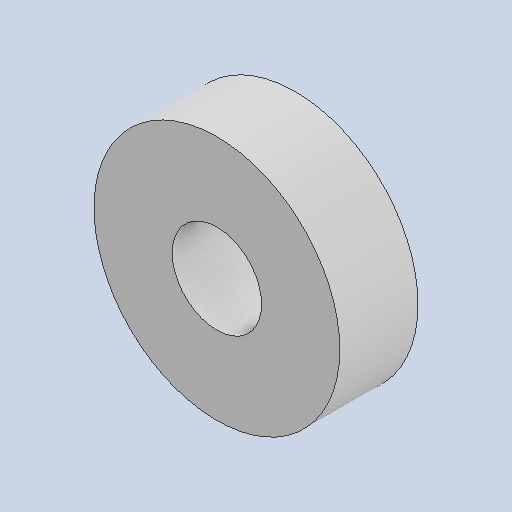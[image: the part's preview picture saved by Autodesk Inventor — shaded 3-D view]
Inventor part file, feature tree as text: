
AUTODESK INVENTOR PART (.ipt)
format: ipt  version: 2022 (Build 260153000, 153)  size: 101,376 bytes
history: native  units: in
note: dims shown in document units (in); Inventor stores cm internally (conversion verified against a paired STEP export)
features: extrude x1, sketch x1
ambient origin geometry x8: Origin, YZ Plane, XZ Plane, XY Plane, X Axis, Y Axis, Z Axis, Center Point
bodies: Solid1 (feature_tree)
feature tree (2):
  extrude  "Extrusion1"  Depth=0.2756in
  sketch  "Sketch1"  dims[d0=0.315in d1=0.8661in d2=0.2756in d3=0.0in]
